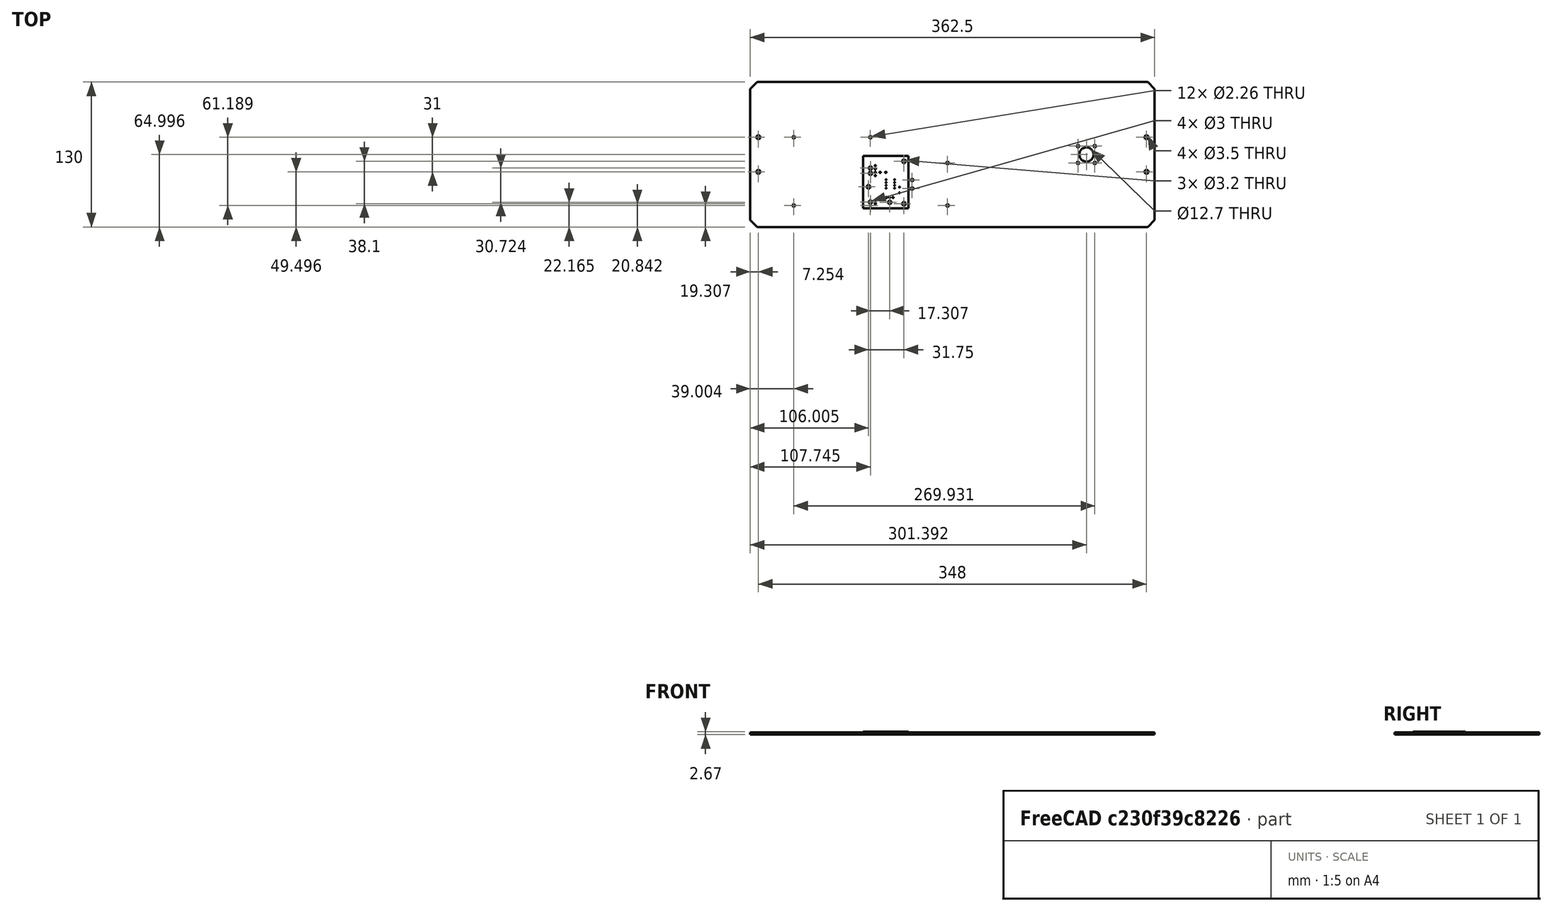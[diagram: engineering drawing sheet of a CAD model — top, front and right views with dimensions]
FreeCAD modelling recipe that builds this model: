
FCSTD DOCUMENT  (FreeCAD 0.20R29603 (Git))
Label: DCT_Back_Panel
License: All rights reserved
LicenseURL: http://en.wikipedia.org/wiki/All_rights_reserved
objects: TechDraw::DrawViewDimension×19, Sketcher::SketchObject×3, PartDesign::Pocket×3, TechDraw::DrawViewAnnotation×3, Part::Feature×2, PartDesign::Line×2, TechDraw::DrawSVGTemplate×2, TechDraw::DrawViewPart×2, TechDraw::DrawPage×2, PartDesign::FeatureBase×1, App::Part×1, PartDesign::ShapeBinder×1, PartDesign::Body×1
note: 16 computed .brp shape members not serialized (recipe doc carries the construction recipe); baked Part::Feature solids carry a one-line shape summary decoded from their .brp

FEATURE [Part::Feature] BaseFeature001  label="Panel001"
  shape: bbox 362.5 x 130 x 2 mm, 14 faces (baked)
FEATURE [PartDesign::FeatureBase] BaseFeature
  BaseFeature = -> BaseFeature001
FEATURE [Sketcher::SketchObject] Sketch005  label="Circular_Connectors001"
  AttachmentOffset = pos=(-152.4,50.8,0) rot=(0,0,1;0rad)
  ExternalGeometry = -> [BaseFeature]
  FullyConstrained = true
  MapMode = 5
  Placement = pos=(-152.4,50.8,71.9309) rot=(0,0,1;0rad)
  Support = -> [BaseFeature]
  sketch-geometry (20):
    g0: LineSegment StartX=314.089 StartY=-117.502 StartZ=0 EndX=334.714 EndY=-117.502 EndZ=0
    g1: LineSegment StartX=334.714 StartY=-117.502 StartZ=0 EndX=334.714 EndY=-138.127 EndZ=0
    g2: LineSegment StartX=334.714 StartY=-138.127 StartZ=0 EndX=314.089 EndY=-138.127 EndZ=0
    g3: LineSegment StartX=314.089 StartY=-138.127 StartZ=0 EndX=314.089 EndY=-117.502 EndZ=0
    g4: Circle CenterX=324.402 CenterY=-127.814 CenterZ=0 NormalX=0 NormalY=0 NormalZ=1 AngleXU=0 Radius=6.35
    g5: Circle CenterX=331.946 CenterY=-120.27 CenterZ=0 NormalX=0 NormalY=0 NormalZ=1 AngleXU=0 Radius=1.1303
    g6: Circle CenterX=331.946 CenterY=-135.358 CenterZ=0 NormalX=0 NormalY=0 NormalZ=1 AngleXU=0 Radius=1.1303
    g7: Circle CenterX=316.858 CenterY=-120.27 CenterZ=0 NormalX=0 NormalY=0 NormalZ=1 AngleXU=0 Radius=1.1303
    g8: Circle CenterX=316.858 CenterY=-135.358 CenterZ=0 NormalX=0 NormalY=0 NormalZ=1 AngleXU=0 Radius=1.1303
    g9: LineSegment StartX=324.402 StartY=-117.502 StartZ=0 EndX=324.402 EndY=-121.464 EndZ=0
    g10: LineSegment StartX=324.402 StartY=-134.164 StartZ=0 EndX=324.402 EndY=-138.127 EndZ=0
    g11: LineSegment StartX=318.052 StartY=-127.814 StartZ=0 EndX=314.089 EndY=-127.814 EndZ=0
    g12: LineSegment StartX=330.752 StartY=-127.814 StartZ=0 EndX=334.714 EndY=-127.814 EndZ=0
    g13: LineSegment StartX=331.946 StartY=-120.27 StartZ=0 EndX=331.946 EndY=-117.502 EndZ=0
    g14: LineSegment StartX=331.946 StartY=-120.27 StartZ=0 EndX=334.714 EndY=-120.27 EndZ=0
    g15: LineSegment StartX=316.858 StartY=-135.358 StartZ=0 EndX=314.089 EndY=-135.358 EndZ=0
    g16: LineSegment StartX=316.858 StartY=-135.358 StartZ=0 EndX=316.858 EndY=-138.127 EndZ=0
    g17: LineSegment StartX=331.946 StartY=-120.27 StartZ=0 EndX=378.264 EndY=-112.314 EndZ=0
    g18: LineSegment StartX=378.264 StartY=-143.314 StartZ=0 EndX=331.946 EndY=-135.358 EndZ=0
    g19: LineSegment StartX=334.714 StartY=-127.814 StartZ=0 EndX=385.514 EndY=-127.814 EndZ=0
  constraints (63):
    c: Coincident(g0,g1)
    c: Coincident(g1,g2)
    c: Coincident(g2,g3)
    c: Coincident(g3,g0)
    c: Horizontal(g0)
    c: Horizontal(g2)
    c: Vertical(g1)
    c: Vertical(g3)
    c: Equal(g2,g1)
    c: PointOnObject(g9,g0)
    c: PointOnObject(g10,g2)
    c: Equal(g6,g8)
    c: Equal(g8,g7)
    c: Equal(g7,g5)
    c: Horizontal(g6,g8)
    c: Vertical(g7,g8)
    c: Horizontal(g7,g5)
    c: DistanceX(g8,g6) = 15.0876
    c: PointOnObject(g9,g4)
    c: Vertical(g9,g9)
    c: Vertical(g6,g5)
    c: PointOnObject(g10,g4)
    c: Vertical(g10,g10)
    c: PointOnObject(g11,g4)
    c: PointOnObject(g11,g3)
    c: Horizontal(g11)
    c: PointOnObject(g12,g4)
    c: PointOnObject(g12,g1)
    c: Horizontal(g12)
    c: Horizontal(g4,g12)
    c: Horizontal(g11,g4)
    c: Vertical(g4,g10)
    c: Coincident(g13,g5)
    c: PointOnObject(g13,g0)
    c: Vertical(g13)
    c: DistanceY(g6,g5) = 15.0876
    c: Coincident(g14,g5)
    c: PointOnObject(g14,g1)
    c: Horizontal(g14)
    c: Equal(g14,g13)
    c: Coincident(g15,g8)
    c: PointOnObject(g15,g3)
    c: Horizontal(g15)
    c: PointOnObject(g16,g15)
    c: PointOnObject(g16,g2)
    c: Vertical(g16)
    c: DistanceX(g15,g8) = 2.7686
    c: Vertical(g16,g8)
    c: Equal(g9,g12)
    c: Equal(g12,g10)
    c: Equal(g10,g11)
    c: Diameter(g4) = 12.7
    c: Diameter(g5) = 2.2606
    c: Coincident(g17,g5)
    c: Coincident(g17,g-3)
    c: Coincident(g18,g-5)
    c: Equal(g17,g18)
    c: Coincident(g18,g6)
    c: DistanceY(g10,g9) = 20.6248
    c: Coincident(g19,g12)
    c: PointOnObject(g19,g-4)
    c: Horizontal(g19)
    c: DistanceX(g19,g19) = 50.8
FEATURE [PartDesign::Pocket] Pocket  label="Power_IN"
  BaseFeature = -> BaseFeature
  Direction = (0,0,-1)
  Length = 5
  Length2 = 5
  Profile = -> Sketch005
  ReferenceAxis = -> Sketch005 [N_Axis]
  Type = 0
FEATURE [Part::Feature] Part__Feature  label="_autosave-SRB PCB"
  Placement = pos=(163,-228,71) rot=(0,0,1;3.14159rad)
  shape: bbox 40.64 x 46.99 x 1.6 mm, 34 faces (baked)
FEATURE [App::Part] SRB_1  label="SRB 1"
  Group = -> [Part__Feature]
  Origin = -> Origin
FEATURE [PartDesign::Line] DatumLine
  AttacherType = Attacher::AttachEngineLine
  Length = 20
  MapMode = 43
  Placement = pos=(51.4984,0,71.9309) rot=(0,0.707107,0.707107;3.14159rad)
  ResizeMode = 0
  Support = -> [Pocket]
FEATURE [PartDesign::Line] DatumLine001
  AttacherType = Attacher::AttachEngineLine
  Length = 20
  MapMode = 44
  Placement = pos=(-1.42e-14,-77.0142,71.9309) rot=(0.57735,0.57735,0.57735;2.0944rad)
  ResizeMode = 0
  Support = -> [Pocket]
FEATURE [Sketcher::SketchObject] Sketch  label="Tripomatic_Mounting_Holes"
  ExternalGeometry = -> [DatumLine,DatumLine001,Pocket]
  FullyConstrained = false
  MapMode = 5
  Placement = pos=(0,0,71.9309) rot=(0,0,1;0rad)
  Support = -> [Pocket]
  sketch-geometry (34):
    g0: LineSegment StartX=-18.4275 StartY=-126.005 StartZ=0 EndX=-93.6877 EndY=-126.005 EndZ=0
    g1: LineSegment StartX=-93.6877 StartY=-126.005 StartZ=0 EndX=-93.6877 EndY=-58.2122 EndZ=0
    g2: LineSegment StartX=-93.6877 StartY=-58.2122 StartZ=0 EndX=-18.4275 EndY=-58.2122 EndZ=0
    g3: LineSegment StartX=-18.4275 StartY=-58.2122 StartZ=0 EndX=-18.4275 EndY=-126.005 EndZ=0
    g4: LineSegment StartX=-122.136 StartY=-92.5142 StartZ=0 EndX=-122.136 EndY=-61.5142 EndZ=0
    g5: GeomPoint X=-122.136 Y=-77.0142 Z=0
    g6: Circle CenterX=-90.3857 CenterY=-122.703 CenterZ=0 NormalX=0 NormalY=0 NormalZ=1 AngleXU=0 Radius=1.5875
    g7: Circle CenterX=-21.7295 CenterY=-122.703 CenterZ=0 NormalX=0 NormalY=0 NormalZ=1 AngleXU=0 Radius=1.5875
    g8: Circle CenterX=-90.3857 CenterY=-61.5142 CenterZ=0 NormalX=0 NormalY=0 NormalZ=1 AngleXU=0 Radius=1.5875
    g9: Circle CenterX=-21.7295 CenterY=-61.5142 CenterZ=0 NormalX=0 NormalY=0 NormalZ=1 AngleXU=0 Radius=1.5875
    g10: LineSegment StartX=-90.3857 StartY=-122.703 StartZ=0 EndX=-90.3857 EndY=-61.5142 EndZ=0
    g11: LineSegment StartX=-21.7295 StartY=-61.5142 StartZ=0 EndX=-21.7295 EndY=-122.703 EndZ=0
    g12: LineSegment StartX=-21.7295 StartY=-122.703 StartZ=0 EndX=-90.3857 EndY=-122.703 EndZ=0
    g13: LineSegment StartX=-90.3857 StartY=-61.5142 StartZ=0 EndX=-21.7295 EndY=-61.5142 EndZ=0
    g14: LineSegment StartX=-21.7295 StartY=-122.703 StartZ=0 EndX=-18.4275 EndY=-126.005 EndZ=0
    g15: LineSegment StartX=-90.3857 StartY=-122.703 StartZ=0 EndX=-93.6877 EndY=-126.005 EndZ=0
    g16: LineSegment StartX=-90.3857 StartY=-61.5142 StartZ=0 EndX=-93.6877 EndY=-58.2122 EndZ=0
    g17: LineSegment StartX=-18.4275 StartY=-58.2122 StartZ=0 EndX=-21.7295 EndY=-61.5142 EndZ=0
    g18: GeomPoint X=-21.7295 Y=-121.115 Z=0
    g19: GeomPoint X=-23.317 Y=-122.703 Z=0
    g20: GeomPoint X=-88.7982 Y=-122.703 Z=0
    g21: GeomPoint X=-90.3857 Y=-121.115 Z=0
    g22: GeomPoint X=-21.7295 Y=-63.1017 Z=0
    g23: LineSegment StartX=225.864 StartY=-92.5142 StartZ=0 EndX=225.864 EndY=-61.5142 EndZ=0
    g24: LineSegment StartX=172.002 StartY=-77.0142 StartZ=0 EndX=225.864 EndY=-77.0142 EndZ=0
    g25: LineSegment StartX=179.546 StartY=-84.558 StartZ=0 EndX=179.546 EndY=-69.4704 EndZ=0
    g26: GeomPoint X=179.546 Y=-77.0142 Z=0
    g27: LineSegment StartX=225.864 StartY=-77.0142 StartZ=0 EndX=202.705 EndY=-77.0142 EndZ=0
    g28: LineSegment StartX=179.546 StartY=-77.0142 StartZ=0 EndX=202.705 EndY=-77.0142 EndZ=0
    g29: Circle CenterX=-21.7295 CenterY=-122.703 CenterZ=0 NormalX=0 NormalY=0 NormalZ=1 AngleXU=0 Radius=1.1303
    g30: Circle CenterX=-90.3857 CenterY=-122.703 CenterZ=0 NormalX=0 NormalY=0 NormalZ=1 AngleXU=0 Radius=1.1303
    g31: Circle CenterX=-90.3857 CenterY=-61.5142 CenterZ=0 NormalX=0 NormalY=0 NormalZ=1 AngleXU=0 Radius=1.1303
    g32: Circle CenterX=-21.7295 CenterY=-61.5142 CenterZ=0 NormalX=0 NormalY=0 NormalZ=1 AngleXU=0 Radius=1.1303
    g33: LineSegment StartX=-21.7295 StartY=-122.703 StartZ=0 EndX=-21.7295 EndY=-126.005 EndZ=0
  constraints (80):
    c: Coincident(g0,g1)
    c: Coincident(g1,g2)
    c: Coincident(g2,g3)
    c: Coincident(g3,g0)
    c: Horizontal(g0)
    c: Horizontal(g2)
    c: Vertical(g1)
    c: Vertical(g3)
    c: DistanceY(g1,g1) = 67.7926
    c: DistanceX(g0,g0) = 75.2602
    c: Coincident(g4,g-5)
    c: Coincident(g4,g-6)
    c: PointOnObject(g5,g-4)
    c: Coincident(g10,g6)
    c: Coincident(g10,g8)
    c: Coincident(g11,g9)
    c: Coincident(g11,g7)
    c: Vertical(g11)
    c: Parallel(g11,g10)
    c: Coincident(g12,g7)
    c: Coincident(g12,g6)
    c: Horizontal(g12)
    c: Coincident(g13,g8)
    c: Coincident(g13,g9)
    c: Horizontal(g13)
    c: Equal(g6,g7)
    c: Equal(g7,g8)
    c: Equal(g8,g9)
    c: Diameter(g6) = 3.175
    c: Coincident(g14,g7)
    c: Coincident(g14,g0)
    c: Coincident(g15,g6)
    c: Coincident(g15,g0)
    c: Coincident(g16,g8)
    c: Coincident(g16,g1)
    c: Coincident(g17,g2)
    c: Coincident(g17,g9)
    c: Equal(g17,g16)
    c: Equal(g16,g15)
    c: Angle(g14,g0) = 0.785398
    c: PointOnObject(g18,g7)
    c: PointOnObject(g19,g7)
    c: PointOnObject(g20,g6)
    c: PointOnObject(g21,g6)
    c: PointOnObject(g21,g10)
    c: PointOnObject(g20,g12)
    c: PointOnObject(g19,g12)
    c: PointOnObject(g18,g11)
    c: DistanceX(g20,g19) = 65.4812
    c: PointOnObject(g22,g9)
    c: PointOnObject(g22,g11)
    c: DistanceY(g18,g22) = 58.0136
    c: Coincident(g23,g-7)
    c: Coincident(g23,g-8)
    c: Coincident(g24,g-9)
    c: PointOnObject(g24,g-4)
    c: PointOnObject(g24,g23)
    c: Coincident(g25,g-11)
    c: PointOnObject(g26,g25)
    c: PointOnObject(g26,g24)
    c: Coincident(g25,g-10)
    c: Coincident(g27,g24)
    c: Coincident(g28,g26)
    c: Coincident(g28,g27)
    c: Equal(g27,g28)
    c: PointOnObject(g27,g24)
    c: DistanceX(g27,g24) = 23.1593
    c: Coincident(g29,g7)
    c: Coincident(g30,g6)
    c: Coincident(g31,g8)
    c: Coincident(g32,g9)
    c: Equal(g32,g31)
    c: Equal(g31,g30)
    c: Equal(g30,g29)
    c: Diameter(g31) = 2.2606
    c: Coincident(g33,g29)
    c: PointOnObject(g33,g0)
    c: Vertical(g33)
    c: Horizontal(g31,g4)
    c: DistanceX(g4,g31) = 31.75
FEATURE [PartDesign::Pocket] Pocket001  label="Tripomatic_Mounting_Holes001"
  BaseFeature = -> Pocket
  Direction = (0,0,-1)
  Length = 5
  Length2 = 5
  Profile = -> Sketch
  ReferenceAxis = -> Sketch [N_Axis]
  Type = 1
FEATURE [PartDesign::ShapeBinder] ShapeBinder  label="SCURV_Shape"
  Placement = pos=(163,-228,71) rot=(0,0,1;3.14159rad)
  Support = -> [Part__Feature]
  TraceSupport = false
FEATURE [Sketcher::SketchObject] Sketch006  label="SCURV_Mounting_Holes"
  ExternalGeometry = -> [ShapeBinder,Pocket001,DatumLine]
  FullyConstrained = true
  MapMode = 5
  Placement = pos=(0,0,71.9309) rot=(0,0,1;0rad)
  Support = -> [Pocket001]
  sketch-geometry (31):
    g0: LineSegment StartX=51.4984 StartY=-126.919 StartZ=0 EndX=10.8584 EndY=-126.919 EndZ=0
    g1: LineSegment StartX=51.4984 StartY=-79.9292 StartZ=0 EndX=51.4984 EndY=-126.919 EndZ=0
    g2: LineSegment StartX=10.8584 StartY=-79.9292 StartZ=0 EndX=51.4984 EndY=-79.9292 EndZ=0
    g3: LineSegment StartX=10.8584 StartY=-126.919 StartZ=0 EndX=10.8584 EndY=-79.9292 EndZ=0
    g4: Circle CenterX=47.4852 CenterY=-84.6028 CenterZ=0 NormalX=0 NormalY=0 NormalZ=1 AngleXU=3.14159 Radius=1.6
    g5: Circle CenterX=15.7352 CenterY=-107.463 CenterZ=0 NormalX=0 NormalY=0 NormalZ=1 AngleXU=3.14159 Radius=1.6
    g6: Circle CenterX=47.4852 CenterY=-122.703 CenterZ=0 NormalX=0 NormalY=0 NormalZ=1 AngleXU=3.14159 Radius=1.6
    g7: LineSegment StartX=8.3648 StartY=-83.0676 StartZ=0 EndX=12.378 EndY=-78.394 EndZ=0
    g8: LineSegment StartX=-23.3852 StartY=-105.928 StartZ=0 EndX=-28.262 EndY=-105.928 EndZ=0
    g9: LineSegment StartX=8.3648 StartY=-121.168 StartZ=0 EndX=12.378 EndY=-125.384 EndZ=0
    g10: LineSegment StartX=15.7352 StartY=-107.463 StartZ=0 EndX=10.8584 EndY=-107.463 EndZ=0
    g11: LineSegment StartX=-21.7295 StartY=-122.703 StartZ=0 EndX=-90.3857 EndY=-122.703 EndZ=0
    g12: LineSegment StartX=8.3648 StartY=-83.0676 StartZ=0 EndX=12.378 EndY=-83.0676 EndZ=0
    g13: LineSegment StartX=8.3648 StartY=-83.0676 StartZ=0 EndX=8.3648 EndY=-78.394 EndZ=0
    g14: LineSegment StartX=47.4852 StartY=-84.6028 StartZ=0 EndX=47.4852 EndY=-79.9292 EndZ=0
    g15: LineSegment StartX=47.4852 StartY=-84.6028 StartZ=0 EndX=51.4984 EndY=-84.6028 EndZ=0
    g16: LineSegment StartX=47.4852 StartY=-122.703 StartZ=0 EndX=51.4984 EndY=-122.703 EndZ=0
    g17: LineSegment StartX=47.4852 StartY=-122.703 StartZ=0 EndX=47.4852 EndY=-126.919 EndZ=0
    g18: LineSegment StartX=8.3648 StartY=-121.168 StartZ=0 EndX=12.378 EndY=-121.168 EndZ=0
    g19: LineSegment StartX=8.3648 StartY=-121.168 StartZ=0 EndX=8.3648 EndY=-125.384 EndZ=0
    g20: Circle CenterX=47.4852 CenterY=-122.703 CenterZ=0 NormalX=0 NormalY=0 NormalZ=1 AngleXU=0 Radius=1.1303
    g21: Circle CenterX=15.7352 CenterY=-107.463 CenterZ=0 NormalX=0 NormalY=0 NormalZ=1 AngleXU=0 Radius=1.1303
    g22: Circle CenterX=47.4852 CenterY=-84.6028 CenterZ=0 NormalX=0 NormalY=0 NormalZ=1 AngleXU=0 Radius=1.1303
    g23: Circle CenterX=14.8716 CenterY=-122.703 CenterZ=0 NormalX=0 NormalY=0 NormalZ=1 AngleXU=0 Radius=1.6
    g24: LineSegment StartX=14.8716 StartY=-122.703 StartZ=0 EndX=14.8716 EndY=-126.919 EndZ=0
    g25: LineSegment StartX=14.8716 StartY=-122.703 StartZ=0 EndX=10.8584 EndY=-122.703 EndZ=0
    g26: Circle CenterX=15.7352 CenterY=-99.8428 CenterZ=0 NormalX=0 NormalY=0 NormalZ=1 AngleXU=0 Radius=1.6
    g27: Circle CenterX=15.7352 CenterY=-99.8428 CenterZ=0 NormalX=0 NormalY=0 NormalZ=1 AngleXU=0 Radius=1.1303
    g28: LineSegment StartX=47.4852 StartY=-122.703 StartZ=0 EndX=47.4852 EndY=-84.6028 EndZ=0
    g29: LineSegment StartX=15.7352 StartY=-107.463 StartZ=0 EndX=47.4852 EndY=-107.463 EndZ=0
    g30: LineSegment StartX=15.7352 StartY=-99.8428 StartZ=0 EndX=47.4852 EndY=-99.8428 EndZ=0
  constraints (89):
    c: Coincident(g0,g1)
    c: Coincident(g1,g2)
    c: Coincident(g2,g3)
    c: Coincident(g3,g0)
    c: Radius(g4) = 1.6
    c: Radius(g5) = 1.6
    c: Equal(g3,g1)
    c: Parallel(g0,g2)
    c: Perpendicular(g2,g3)
    c: PointOnObject(g8,g-6)
    c: Horizontal(g8)
    c: Coincident(g-7,g8)
    c: Coincident(g9,g-5)
    c: Coincident(g9,g-8)
    c: Coincident(g-9,g7)
    c: Coincident(g7,g-4)
    c: Equal(g2,g-3)
    c: Equal(g3,g-6)
    c: PointOnObject(g10,g3)
    c: Horizontal(g0)
    c: Coincident(g10,g5)
    c: Horizontal(g10)
    c: Equal(g10,g8)
    c: Angle(g-3,g7) = 0.861276
    c: Coincident(g11,g-10)
    c: Coincident(g11,g-11)
    c: Horizontal(g6,g11)
    c: DistanceY(g-6,g8) = 19.4564
    c: DistanceY(g0,g10) = 19.4564
    c: Coincident(g12,g7)
    c: Coincident(g13,g7)
    c: PointOnObject(g12,g-4)
    c: PointOnObject(g13,g-3)
    c: Vertical(g13)
    c: Horizontal(g12)
    c: Equal(g14,g13)
    c: PointOnObject(g14,g2)
    c: PointOnObject(g15,g1)
    c: Horizontal(g15)
    c: Vertical(g14)
    c: Equal(g12,g15)
    c: Coincident(g16,g6)
    c: Coincident(g17,g6)
    c: PointOnObject(g17,g0)
    c: PointOnObject(g16,g1)
    c: Horizontal(g16)
    c: Vertical(g17)
    c: PointOnObject(g18,g-4)
    c: PointOnObject(g19,g-5)
    c: Coincident(g19,g9)
    c: Coincident(g18,g9)
    c: Vertical(g19)
    c: Horizontal(g18)
    c: Equal(g19,g17)
    c: Equal(g18,g16)
    c: Coincident(g14,g15)
    c: Coincident(g4,g14)
    c: Coincident(g20,g6)
    c: Equal(g21,g20)
    c: Equal(g20,g22)
    c: Diameter(g22) = 2.2606
    c: Coincident(g21,g5)
    c: Coincident(g22,g4)
    c: Horizontal(g25)
    c: PointOnObject(g25,g3)
    c: PointOnObject(g24,g0)
    c: Vertical(g24)
    c: Equal(g23,g6)
    c: Equal(g25,g16)
    c: Equal(g24,g17)
    c: Coincident(g25,g24)
    c: Coincident(g23,g24)
    c: Equal(g23,g-8)
    c: PointOnObject(g0,g-12)
    c: DistanceX(g11,g9) = 30.0943
    c: Coincident(g27,g26)
    c: Vertical(g26,g21)
    c: Coincident(g28,g20)
    c: Coincident(g28,g22)
    c: Coincident(g29,g21)
    c: PointOnObject(g29,g28)
    c: Horizontal(g29)
    c: Equal(g26,g5)
    c: Equal(g27,g21)
    c: Coincident(g30,g27)
    c: PointOnObject(g30,g28)
    c: Horizontal(g30)
    c: DistanceY(g20,g29) = 15.24
    c: DistanceY(g30,g22) = 15.24
FEATURE [PartDesign::Pocket] Pocket002  label="SCUR-V_mounting_Holes"
  BaseFeature = -> Pocket001
  Direction = (0,0,-1)
  Length = 5
  Length2 = 5
  Profile = -> Sketch006
  ReferenceAxis = -> Sketch006 [N_Axis]
  Type = 1
FEATURE [PartDesign::Body] Body001  label="Body"
  BaseFeature = -> BaseFeature001
  Group = -> [BaseFeature,Sketch005,Pocket,DatumLine,DatumLine001,Sketch,Pocket001,Sketch006,ShapeBinder,Pocket002]
  Origin = -> Origin001
  Tip = -> Pocket002
FEATURE [TechDraw::DrawSVGTemplate] Template001
  EditableTexts = AUTHOR_NAME=Dennis H. Calderon; DRAWING_TITLE=DCT_HSK_Back_Panel; FC-DATE=03/16/2023; FC-REV=REV A; FC-SH=1/1; FC-SI=A4; FreeCAD_DRAWING=HELIX; SI-1=The Ohio State University
  Height = 210
  Orientation = 1
  Width = 297
FEATURE [TechDraw::DrawViewPart] View001
  CoarseView = false
  Direction = (0,0,1)
  Focus = 100
  HardHidden = false
  IsoCount = 0
  IsoHidden = false
  IsoVisible = false
  LockPosition = false
  Perspective = false
  Rotation = 0
  Scale = 0.6
  ScaleType = 2
  SeamHidden = false
  SeamVisible = true
  SmoothHidden = false
  SmoothVisible = true
  Source = -> [Body001]
  X = 150.001
  XDirection = (-1,0,0)
  Y = 122.605
FEATURE [TechDraw::DrawViewAnnotation] Annotation001
  Font = osifont
  LineSpace = 80
  LockPosition = false
  MaxWidth = -1
  Rotation = 0
  ScaleType = 0
  Text = All holes measuring 0.089" | to be tapped to fit | #4-40 threaded screws. | Holes with a "cross-hair"  | measure to be 0.089"  | except when otherwise noted
  TextSize = 5.08
  TextStyle = 0
  X = 46.4167
  Y = 34.2969
FEATURE [TechDraw::DrawViewDimension] Dimension030
  AngleOverride = false
  Arbitrary = false
  ArbitraryTolerances = false
  EqualTolerance = true
  ExtensionAngle = 0
  FormatSpec = ⌀%.3w
  FormatSpecOverTolerance = %+.2w
  FormatSpecUnderTolerance = %+.2w
  Inverted = false
  LineAngle = 0
  LockPosition = false
  MeasureType = 1
  OverTolerance = 0
  References2D = -> [View001]
  Rotation = 0
  ScaleType = 0
  TheoreticalExact = false
  Type = 5
  UnderTolerance = 0
  X = 88.1361
  Y = -20.1468
FEATURE [TechDraw::DrawViewDimension] Dimension031
  AngleOverride = false
  Arbitrary = false
  ArbitraryTolerances = false
  EqualTolerance = true
  ExtensionAngle = 0
  FormatSpec = ⌀%.3w
  FormatSpecOverTolerance = %+.2w
  FormatSpecUnderTolerance = %+.2w
  Inverted = false
  LineAngle = 0
  LockPosition = false
  MeasureType = 1
  OverTolerance = 0
  References2D = -> [View001]
  Rotation = 0
  ScaleType = 0
  TheoreticalExact = false
  Type = 5
  UnderTolerance = 0
  X = -120.623
  Y = 10.1032
FEATURE [TechDraw::DrawViewDimension] Dimension037
  AngleOverride = false
  Arbitrary = false
  ArbitraryTolerances = false
  EqualTolerance = true
  ExtensionAngle = 0
  FormatSpec = %.2w
  FormatSpecOverTolerance = %+.2w
  FormatSpecUnderTolerance = %+.2w
  Inverted = false
  LineAngle = 0
  LockPosition = false
  MeasureType = 1
  OverTolerance = 0
  References2D = -> [View001]
  Rotation = 0
  ScaleType = 0
  TheoreticalExact = false
  Type = 2
  UnderTolerance = 0
  X = 121.77
  Y = -19.329
FEATURE [TechDraw::DrawPage] Page  label="DCT_HSK_Back_Panel_Drawing"
  KeepUpdated = true
  NextBalloonIndex = 1
  ProjectionType = 0
  Template = -> Template001
  Views = -> [View001,Annotation001,Dimension030,Dimension031,Dimension037]
FEATURE [TechDraw::DrawSVGTemplate] Template
  EditableTexts = AUTHOR_NAME=Dennis H. Calderon; DATE=03/30/2023; REVISION=REV 2; SIZE=A4; TITLELINE-1=DCT_HSK_Box_Back_Panel; TITLELINE-2=HELIX; TITLELINE-3=The Ohio State University
  Height = 210
  Orientation = 1
  Width = 297
FEATURE [TechDraw::DrawViewPart] View
  CoarseView = false
  Direction = (0,0,-1)
  Focus = 100
  HardHidden = false
  IsoCount = 0
  IsoHidden = false
  IsoVisible = false
  LockPosition = false
  Perspective = false
  Rotation = 0
  Scale = 0.6
  ScaleType = 0
  SeamHidden = false
  SeamVisible = true
  SmoothHidden = false
  SmoothVisible = true
  Source = -> [Pocket002]
  X = 151.031
  XDirection = (1,0,0)
  Y = 123.409
FEATURE [TechDraw::DrawViewAnnotation] Annotation
  Font = osifont
  LineSpace = 80
  LockPosition = false
  MaxWidth = -1
  Rotation = 0
  Scale = 0.6
  ScaleType = 0
  Text = All holes measuring  | to be 0.089 inches |  to be tapped  | to fit #4-40 screw
  TextSize = 5.08
  TextStyle = 0
  X = 32.9376
  Y = 21.6931
FEATURE [TechDraw::DrawViewDimension] Dimension
  AngleOverride = false
  Arbitrary = false
  ArbitraryTolerances = false
  EqualTolerance = true
  ExtensionAngle = 0
  FormatSpec = %.2w
  FormatSpecOverTolerance = %+.2w
  FormatSpecUnderTolerance = %+.2w
  Inverted = false
  LineAngle = 0
  LockPosition = false
  MeasureType = 1
  OverTolerance = 0
  References2D = -> [View]
  Rotation = 0
  Scale = 0.6
  ScaleType = 0
  TheoreticalExact = false
  Type = 1
  UnderTolerance = 0
  X = -98.302
  Y = 53.6074
FEATURE [TechDraw::DrawViewDimension] Dimension038
  AngleOverride = false
  Arbitrary = false
  ArbitraryTolerances = false
  EqualTolerance = true
  ExtensionAngle = 0
  FormatSpec = %.2w
  FormatSpecOverTolerance = %+.2w
  FormatSpecUnderTolerance = %+.2w
  Inverted = false
  LineAngle = 0
  LockPosition = false
  MeasureType = 1
  OverTolerance = 0
  References2D = -> [View]
  Rotation = 0
  Scale = 0.6
  ScaleType = 0
  TheoreticalExact = false
  Type = 2
  UnderTolerance = 0
  X = -67.662
  Y = 61.3027
FEATURE [TechDraw::DrawViewDimension] Dimension039
  AngleOverride = false
  Arbitrary = false
  ArbitraryTolerances = false
  EqualTolerance = true
  ExtensionAngle = 0
  FormatSpec = %.2w
  FormatSpecOverTolerance = %+.2w
  FormatSpecUnderTolerance = %+.2w
  Inverted = false
  LineAngle = 0
  LockPosition = false
  MeasureType = 1
  OverTolerance = 0
  References2D = -> [View]
  Rotation = 0
  Scale = 0.6
  ScaleType = 0
  TheoreticalExact = false
  Type = 1
  UnderTolerance = 0
  X = -65.209
  Y = -17.7578
FEATURE [TechDraw::DrawViewDimension] Dimension040
  AngleOverride = false
  Arbitrary = false
  ArbitraryTolerances = false
  EqualTolerance = true
  ExtensionAngle = 0
  FormatSpec = ⌀%.3w
  FormatSpecOverTolerance = %+.2w
  FormatSpecUnderTolerance = %+.2w
  Inverted = false
  LineAngle = 0
  LockPosition = false
  MeasureType = 1
  OverTolerance = 0
  References2D = -> [View]
  Rotation = 0
  Scale = 0.6
  ScaleType = 0
  TheoreticalExact = false
  Type = 5
  UnderTolerance = 0
  X = -30.3945
  Y = 55.1376
FEATURE [TechDraw::DrawViewDimension] Dimension041
  AngleOverride = false
  Arbitrary = false
  ArbitraryTolerances = false
  EqualTolerance = true
  ExtensionAngle = 0
  FormatSpec = %.2w
  FormatSpecOverTolerance = %+.2w
  FormatSpecUnderTolerance = %+.2w
  Inverted = false
  LineAngle = 0
  LockPosition = false
  MeasureType = 1
  OverTolerance = 0
  References2D = -> [View]
  Rotation = 0
  Scale = 0.6
  ScaleType = 0
  TheoreticalExact = false
  Type = 2
  UnderTolerance = 0
  X = 5.32694
  Y = 53.246
FEATURE [TechDraw::DrawViewDimension] Dimension042
  AngleOverride = false
  Arbitrary = false
  ArbitraryTolerances = false
  EqualTolerance = true
  ExtensionAngle = 0
  FormatSpec = %.2w
  FormatSpecOverTolerance = %+.2w
  FormatSpecUnderTolerance = %+.2w
  Inverted = false
  LineAngle = 0
  LockPosition = false
  MeasureType = 1
  OverTolerance = 0
  References2D = -> [View]
  Rotation = 0
  Scale = 0.6
  ScaleType = 0
  TheoreticalExact = false
  Type = 1
  UnderTolerance = 0
  X = -11.0093
  Y = 38.0441
FEATURE [TechDraw::DrawViewDimension] Dimension043
  AngleOverride = false
  Arbitrary = false
  ArbitraryTolerances = false
  EqualTolerance = true
  ExtensionAngle = 0
  FormatSpec = %.2w
  FormatSpecOverTolerance = %+.2w
  FormatSpecUnderTolerance = %+.2w
  Inverted = false
  LineAngle = 0
  LockPosition = false
  MeasureType = 1
  OverTolerance = 0
  References2D = -> [View]
  Rotation = 0
  Scale = 0.6
  ScaleType = 0
  TheoreticalExact = false
  Type = 2
  UnderTolerance = 0
  X = -34.0365
  Y = 19.5784
FEATURE [TechDraw::DrawViewDimension] Dimension044
  AngleOverride = false
  Arbitrary = false
  ArbitraryTolerances = false
  EqualTolerance = true
  ExtensionAngle = 0
  FormatSpec = %.2w
  FormatSpecOverTolerance = %+.2w
  FormatSpecUnderTolerance = %+.2w
  Inverted = false
  LineAngle = 0
  LockPosition = false
  MeasureType = 1
  OverTolerance = 0
  References2D = -> [View]
  Rotation = 0
  Scale = 0.6
  ScaleType = 0
  TheoreticalExact = false
  Type = 1
  UnderTolerance = 0
  X = 50.63
  Y = -13.1738
FEATURE [TechDraw::DrawViewDimension] Dimension045
  AngleOverride = false
  Arbitrary = false
  ArbitraryTolerances = false
  EqualTolerance = true
  ExtensionAngle = 0
  FormatSpec = %.2w
  FormatSpecOverTolerance = %+.2w
  FormatSpecUnderTolerance = %+.2w
  Inverted = false
  LineAngle = 0
  LockPosition = false
  MeasureType = 1
  OverTolerance = 0
  References2D = -> [View]
  Rotation = 0
  Scale = 0.6
  ScaleType = 0
  TheoreticalExact = false
  Type = 2
  UnderTolerance = 0
  X = 16.8121
  Y = 18.0608
FEATURE [TechDraw::DrawViewDimension] Dimension046
  AngleOverride = false
  Arbitrary = false
  ArbitraryTolerances = false
  EqualTolerance = true
  ExtensionAngle = 0
  FormatSpec = %.2w
  FormatSpecOverTolerance = %+.2w
  FormatSpecUnderTolerance = %+.2w
  Inverted = false
  LineAngle = 0
  LockPosition = false
  MeasureType = 1
  OverTolerance = 0
  References2D = -> [View]
  Rotation = 0
  Scale = 0.6
  ScaleType = 0
  TheoreticalExact = false
  Type = 2
  UnderTolerance = 0
  X = 1.60347
  Y = 14.9775
FEATURE [TechDraw::DrawViewDimension] Dimension047
  AngleOverride = false
  Arbitrary = false
  ArbitraryTolerances = false
  EqualTolerance = true
  ExtensionAngle = 0
  FormatSpec = %.2w
  FormatSpecOverTolerance = %+.2w
  FormatSpecUnderTolerance = %+.2w
  Inverted = false
  LineAngle = 0
  LockPosition = false
  MeasureType = 1
  OverTolerance = 0
  References2D = -> [View]
  Rotation = 0
  Scale = 0.6
  ScaleType = 0
  TheoreticalExact = false
  Type = 2
  UnderTolerance = 0
  X = -95.436
  Y = 12.5083
FEATURE [TechDraw::DrawViewDimension] Dimension048
  AngleOverride = false
  Arbitrary = false
  ArbitraryTolerances = false
  EqualTolerance = true
  ExtensionAngle = 0
  FormatSpec = ⌀%.2w
  FormatSpecOverTolerance = %+.2w
  FormatSpecUnderTolerance = %+.2w
  Inverted = false
  LineAngle = 0
  LockPosition = false
  MeasureType = 1
  OverTolerance = 0
  References2D = -> [View]
  Rotation = 0
  Scale = 0.6
  ScaleType = 0
  TheoreticalExact = false
  Type = 5
  UnderTolerance = 0
  X = 89.6799
  Y = -3.24811
FEATURE [TechDraw::DrawViewDimension] Dimension049
  AngleOverride = false
  Arbitrary = false
  ArbitraryTolerances = false
  EqualTolerance = true
  ExtensionAngle = 0
  FormatSpec = %.2w
  FormatSpecOverTolerance = %+.2w
  FormatSpecUnderTolerance = %+.2w
  Inverted = false
  LineAngle = 0
  LockPosition = false
  MeasureType = 1
  OverTolerance = 0
  References2D = -> [View]
  Rotation = 0
  Scale = 0.6
  ScaleType = 0
  TheoreticalExact = false
  Type = 1
  UnderTolerance = 0
  X = 76.542
  Y = 20.372
FEATURE [TechDraw::DrawViewDimension] Dimension050
  AngleOverride = false
  Arbitrary = false
  ArbitraryTolerances = false
  EqualTolerance = true
  ExtensionAngle = 0
  FormatSpec = %.2w
  FormatSpecOverTolerance = %+.2w
  FormatSpecUnderTolerance = %+.2w
  Inverted = false
  LineAngle = 0
  LockPosition = false
  MeasureType = 1
  OverTolerance = 0
  References2D = -> [View]
  Rotation = 0
  Scale = 0.6
  ScaleType = 0
  TheoreticalExact = false
  Type = 1
  UnderTolerance = 0
  X = 88.1259
  Y = -20.9088
FEATURE [TechDraw::DrawViewDimension] Dimension051
  AngleOverride = false
  Arbitrary = false
  ArbitraryTolerances = false
  EqualTolerance = true
  ExtensionAngle = 0
  FormatSpec = %.2w
  FormatSpecOverTolerance = %+.2w
  FormatSpecUnderTolerance = %+.2w
  Inverted = false
  LineAngle = 0
  LockPosition = false
  MeasureType = 1
  OverTolerance = 0
  References2D = -> [View]
  Rotation = 0
  Scale = 0.6
  ScaleType = 0
  TheoreticalExact = false
  Type = 2
  UnderTolerance = 0
  X = 94.3037
  Y = 20.5205
FEATURE [TechDraw::DrawViewDimension] Dimension052
  AngleOverride = false
  Arbitrary = false
  ArbitraryTolerances = false
  EqualTolerance = true
  ExtensionAngle = 0
  FormatSpec = %.2w
  FormatSpecOverTolerance = %+.2w
  FormatSpecUnderTolerance = %+.2w
  Inverted = false
  LineAngle = 0
  LockPosition = false
  MeasureType = 1
  OverTolerance = 0
  References2D = -> [View]
  Rotation = 0
  Scale = 0.6
  ScaleType = 0
  TheoreticalExact = false
  Type = 2
  UnderTolerance = 0
  X = 53.2642
  Y = 3.85464
FEATURE [TechDraw::DrawViewAnnotation] Annotation002
  Font = osifont
  LineSpace = 80
  LockPosition = false
  MaxWidth = -1
  Rotation = 0
  Scale = 0.6
  ScaleType = 0
  Text = All holes with a "crosshair" | are measered to be 0.089 inches | unless otherwise noted
  TextSize = 5.08
  TextStyle = 0
  X = 46.6755
  Y = 51.2114
FEATURE [TechDraw::DrawPage] Page001  label="Drawing_DCT_HSK_Back_Panel"
  KeepUpdated = true
  NextBalloonIndex = 1
  ProjectionType = 0
  Scale = 0.6
  Template = -> Template
  Views = -> [View,Annotation,Dimension,Dimension038,Dimension039,Dimension040,Dimension041,Dimension042,Dimension043,Dimension044,Dimension045,Dimension046,Dimension047,Dimension048,Dimension049,Dimension050,Dimension051,Dimension052,Annotation002]
